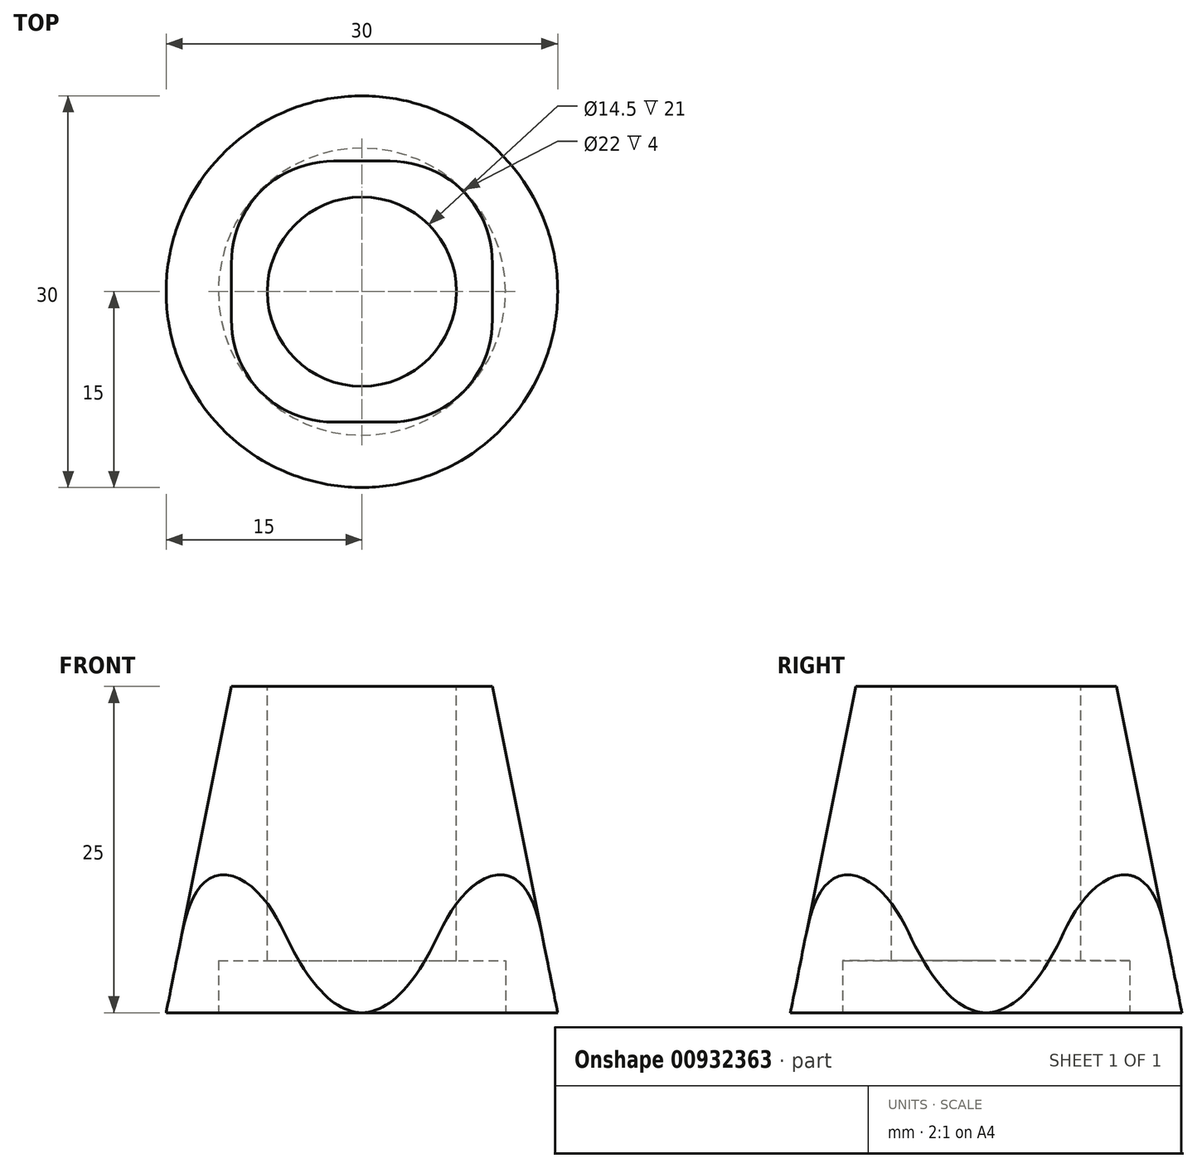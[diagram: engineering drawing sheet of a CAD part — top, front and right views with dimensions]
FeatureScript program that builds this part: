
annotation { "Feature Type Name" : "Feature", "Feature Type Description" : "" }
export const myFeature = defineFeature(function(context is Context, id is Id, definition is map)
    precondition{}
    {
        {
            var Q0;
            Q0=qCreatedBy(makeId("Top.planeOp"),FACE);
            var sketch = newSketch(context, id + "F0", { "sketchPlane" : qUnion([Q0])});
            skLineSegment(sketch, "E0.bottom", {"start": v(15, 15) * mm, "end": v(-15, 15) * mm});
            skLineSegment(sketch, "E0.top", {"start": v(15, -15) * mm, "end": v(-15, -15) * mm});
            skLineSegment(sketch, "E0.left", {"start": v(15, 15) * mm, "end": v(15, -15) * mm});
            skLineSegment(sketch, "E0.right", {"start": v(-15, 15) * mm, "end": v(-15, -15) * mm});
            skPoint(sketch, "E0.middle", {"position": v(0, 0) * mm});
            skSolve(sketch);
        }
        {
            var Q0;
            Q0 = qSketchRegion(id + "F0", true);
            extrude(context, id + "F1", {"entities" : qUnion([Q0]), "depth" : 25 * mm, "offsetDistance" : 25 * mm});
        }
        {
            var Q0;
            Q0=makeQuery(id+"F1.opExtrude","CAP_FACE",FACE,{"disambiguationData":[OSD([sQuery(id+"F0.wireOp",EDGE,"E0.bottom"),sQuery(id+"F0.wireOp",EDGE,"E0.top"),sQuery(id+"F0.wireOp",EDGE,"E0.left"),sQuery(id+"F0.wireOp",EDGE,"E0.right")])],"isStart":false});
            var sketch = newSketch(context, id + "F2", { "sketchPlane" : qUnion([Q0])});
            skCircle(sketch, "E1", {"center": v(0, 0) * mm, "radius": 7.25 * mm});
            skSolve(sketch);
        }
        {
            var Q0;
            Q0 = qSketchRegion(id + "F2", true);
            extrude(context, id + "F3", {"entities" : qUnion([Q0]), "operationType" : NewBodyOperationType.REMOVE, "oppositeDirection" : true, "depth" : 25 * mm, "offsetDistance" : 25 * mm});
        }
        {
            var Q0;
            Q0=makeQuery(id+"F1.opExtrude","CAP_EDGE",EDGE,{"disambiguationData":[OSD([sQuery(id+"F0.wireOp",EDGE,"E0.left")])],"isStart":false});
            var Q1;
            Q1=makeQuery(id+"F1.opExtrude","CAP_EDGE",EDGE,{"disambiguationData":[OSD([sQuery(id+"F0.wireOp",EDGE,"E0.bottom")])],"isStart":false});
            var Q2;
            Q2=makeQuery(id+"F1.opExtrude","CAP_EDGE",EDGE,{"disambiguationData":[OSD([sQuery(id+"F0.wireOp",EDGE,"E0.right")])],"isStart":false});
            var Q3;
            Q3=makeQuery(id+"F1.opExtrude","CAP_EDGE",EDGE,{"disambiguationData":[OSD([sQuery(id+"F0.wireOp",EDGE,"E0.top")])],"isStart":false});
            chamfer(context, id + "F4", {"entities" : qUnion([Q0, Q1, Q2, Q3]), "chamferType" : ChamferType.TWO_OFFSETS, "width1" : 25 * mm, "oppositeDirection" : false, "width2" : 5 * mm, "tangentPropagation" : true});
        }
        {
            var Q0;
            Q0=makeQuery(id+"F4.opChamfer","BLEND_EDGE",EDGE,{"blendedFrom":[makeQuery(id+"F1.opExtrude","CAP_EDGE",EDGE,{"disambiguationData":[OSD([sQuery(id+"F0.wireOp",EDGE,"E0.top")])],"isStart":false}),makeQuery(id+"F1.opExtrude","CAP_EDGE",EDGE,{"disambiguationData":[OSD([sQuery(id+"F0.wireOp",EDGE,"E0.left")])],"isStart":false})],"blendedInto":[]});
            var Q1;
            Q1=makeQuery(id+"F4.opChamfer","BLEND_EDGE",EDGE,{"blendedFrom":[makeQuery(id+"F1.opExtrude","CAP_EDGE",EDGE,{"disambiguationData":[OSD([sQuery(id+"F0.wireOp",EDGE,"E0.bottom")])],"isStart":false}),makeQuery(id+"F1.opExtrude","CAP_EDGE",EDGE,{"disambiguationData":[OSD([sQuery(id+"F0.wireOp",EDGE,"E0.left")])],"isStart":false})],"blendedInto":[]});
            var Q2;
            Q2=makeQuery(id+"F4.opChamfer","BLEND_EDGE",EDGE,{"blendedFrom":[makeQuery(id+"F1.opExtrude","CAP_EDGE",EDGE,{"disambiguationData":[OSD([sQuery(id+"F0.wireOp",EDGE,"E0.bottom")])],"isStart":false}),makeQuery(id+"F1.opExtrude","CAP_EDGE",EDGE,{"disambiguationData":[OSD([sQuery(id+"F0.wireOp",EDGE,"E0.right")])],"isStart":false})],"blendedInto":[]});
            var Q3;
            Q3=makeQuery(id+"F4.opChamfer","BLEND_EDGE",EDGE,{"blendedFrom":[makeQuery(id+"F1.opExtrude","CAP_EDGE",EDGE,{"disambiguationData":[OSD([sQuery(id+"F0.wireOp",EDGE,"E0.top")])],"isStart":false}),makeQuery(id+"F1.opExtrude","CAP_EDGE",EDGE,{"disambiguationData":[OSD([sQuery(id+"F0.wireOp",EDGE,"E0.right")])],"isStart":false})],"blendedInto":[]});
            fillet(context, id + "F5", {"entities" : qUnion([Q0, Q1, Q2, Q3]), "radius" : 8 * mm, "tangentPropagation" : true, "allowEdgeOverflow" : false});
        }
        {
            var Q0;
            Q0=makeQuery(id+"F1.opExtrude","CAP_FACE",FACE,{"disambiguationData":[OSD([sQuery(id+"F0.wireOp",EDGE,"E0.bottom"),sQuery(id+"F0.wireOp",EDGE,"E0.top"),sQuery(id+"F0.wireOp",EDGE,"E0.left"),sQuery(id+"F0.wireOp",EDGE,"E0.right")])],"isStart":true});
            var sketch = newSketch(context, id + "F6", { "sketchPlane" : qUnion([Q0])});
            skCircle(sketch, "E2", {"center": v(0, 0) * mm, "radius": 15 * mm});
            skSolve(sketch);
        }
        {
            var Q0;
            {var subQ1=sQuery(id+"F0.wireOp",EDGE,"E0.left");var subQ2=sQuery(id+"F0.wireOp",EDGE,"E0.top");var subQ3=makeQuery(id+"F1.opExtrude","CAP_FACE",FACE,{"disambiguationData":[OSD([sQuery(id+"F0.wireOp",EDGE,"E0.bottom"),subQ2,subQ1,sQuery(id+"F0.wireOp",EDGE,"E0.right")])],"isStart":true});var subQ4=makeQuery(id+"F1.opExtrude","CAP_EDGE",EDGE,{"disambiguationData":[OSD([subQ2])],"isStart":false});var subQ7=makeQuery(id+"F1.opExtrude","CAP_EDGE",EDGE,{"disambiguationData":[OSD([subQ1])],"isStart":false});var subQ10=makeQuery(id+"F5.opFillet","BLEND_EDGE",EDGE,{"blendedFrom":[makeQuery(id+"F4.opChamfer","BLEND_EDGE",EDGE,{"blendedFrom":[subQ4,subQ7],"blendedInto":[]}),subQ3],"blendedInto":[subQ3]});Q0=makeQuery(id+"F6.imprint","IMPRINT",FACE,{"disambiguationData":[TD([[makeQuery(id+"F6.imprint","IMPRINT",EDGE,{"derivedFrom":subQ10}),1.0]])]});}
            var Q1;
            {var subQ1=sQuery(id+"F0.wireOp",EDGE,"E0.right");var subQ2=sQuery(id+"F0.wireOp",EDGE,"E0.top");var subQ3=makeQuery(id+"F1.opExtrude","CAP_FACE",FACE,{"disambiguationData":[OSD([sQuery(id+"F0.wireOp",EDGE,"E0.bottom"),subQ2,sQuery(id+"F0.wireOp",EDGE,"E0.left"),subQ1])],"isStart":true});var subQ4=makeQuery(id+"F1.opExtrude","CAP_EDGE",EDGE,{"disambiguationData":[OSD([subQ2])],"isStart":false});var subQ7=makeQuery(id+"F1.opExtrude","CAP_EDGE",EDGE,{"disambiguationData":[OSD([subQ1])],"isStart":false});var subQ10=makeQuery(id+"F5.opFillet","BLEND_EDGE",EDGE,{"blendedFrom":[makeQuery(id+"F4.opChamfer","BLEND_EDGE",EDGE,{"blendedFrom":[subQ4,subQ7],"blendedInto":[]}),subQ3],"blendedInto":[subQ3]});Q1=makeQuery(id+"F6.imprint","IMPRINT",FACE,{"disambiguationData":[TD([[makeQuery(id+"F6.imprint","IMPRINT",EDGE,{"derivedFrom":subQ10}),1.0]])]});}
            var Q2;
            {var subQ1=sQuery(id+"F0.wireOp",EDGE,"E0.right");var subQ2=sQuery(id+"F0.wireOp",EDGE,"E0.bottom");var subQ3=makeQuery(id+"F1.opExtrude","CAP_FACE",FACE,{"disambiguationData":[OSD([subQ2,sQuery(id+"F0.wireOp",EDGE,"E0.top"),sQuery(id+"F0.wireOp",EDGE,"E0.left"),subQ1])],"isStart":true});var subQ4=makeQuery(id+"F1.opExtrude","CAP_EDGE",EDGE,{"disambiguationData":[OSD([subQ1])],"isStart":false});var subQ7=makeQuery(id+"F1.opExtrude","CAP_EDGE",EDGE,{"disambiguationData":[OSD([subQ2])],"isStart":false});var subQ10=makeQuery(id+"F5.opFillet","BLEND_EDGE",EDGE,{"blendedFrom":[makeQuery(id+"F4.opChamfer","BLEND_EDGE",EDGE,{"blendedFrom":[subQ7,subQ4],"blendedInto":[]}),subQ3],"blendedInto":[subQ3]});Q2=makeQuery(id+"F6.imprint","IMPRINT",FACE,{"disambiguationData":[TD([[makeQuery(id+"F6.imprint","IMPRINT",EDGE,{"derivedFrom":subQ10}),1.0]])]});}
            var Q3;
            {var subQ1=sQuery(id+"F0.wireOp",EDGE,"E0.left");var subQ2=sQuery(id+"F0.wireOp",EDGE,"E0.bottom");var subQ3=makeQuery(id+"F1.opExtrude","CAP_FACE",FACE,{"disambiguationData":[OSD([subQ2,sQuery(id+"F0.wireOp",EDGE,"E0.top"),subQ1,sQuery(id+"F0.wireOp",EDGE,"E0.right")])],"isStart":true});var subQ4=makeQuery(id+"F1.opExtrude","CAP_EDGE",EDGE,{"disambiguationData":[OSD([subQ1])],"isStart":false});var subQ7=makeQuery(id+"F1.opExtrude","CAP_EDGE",EDGE,{"disambiguationData":[OSD([subQ2])],"isStart":false});var subQ10=makeQuery(id+"F5.opFillet","BLEND_EDGE",EDGE,{"blendedFrom":[makeQuery(id+"F4.opChamfer","BLEND_EDGE",EDGE,{"blendedFrom":[subQ7,subQ4],"blendedInto":[]}),subQ3],"blendedInto":[subQ3]});Q3=makeQuery(id+"F6.imprint","IMPRINT",FACE,{"disambiguationData":[TD([[makeQuery(id+"F6.imprint","IMPRINT",EDGE,{"derivedFrom":subQ10}),1.0]])]});}
            extrude(context, id + "F7", {"entities" : qUnion([Q0, Q1, Q2, Q3]), "operationType" : NewBodyOperationType.REMOVE, "oppositeDirection" : true, "depth" : 25 * mm, "offsetDistance" : 25 * mm});
        }
        {
            var Q0;
            Q0=makeQuery(id+"F1.opExtrude","CAP_FACE",FACE,{"disambiguationData":[OSD([sQuery(id+"F0.wireOp",EDGE,"E0.bottom"),sQuery(id+"F0.wireOp",EDGE,"E0.top"),sQuery(id+"F0.wireOp",EDGE,"E0.left"),sQuery(id+"F0.wireOp",EDGE,"E0.right")])],"isStart":true});
            var sketch = newSketch(context, id + "F8", { "sketchPlane" : qUnion([Q0])});
            skCircle(sketch, "E3", {"center": v(0, 0) * mm, "radius": 11 * mm});
            skSolve(sketch);
        }
        {
            var Q0;
            Q0 = qSketchRegion(id + "F8", true);
            extrude(context, id + "F9", {"entities" : qUnion([Q0]), "operationType" : NewBodyOperationType.REMOVE, "oppositeDirection" : true, "depth" : 4 * mm, "offsetDistance" : 25 * mm});
        }
    });
